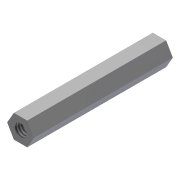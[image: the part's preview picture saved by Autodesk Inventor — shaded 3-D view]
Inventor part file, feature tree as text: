
AUTODESK INVENTOR PART (.ipt)
format: ipt  version: 2013 (Build 170138000, 138)  size: 79,872 bytes
history: native  units: in
note: dims shown in document units (in); Inventor stores cm internally (conversion verified against a paired STEP export)
features: sketch x2, extrude x1, hole x1, mirror x1
ambient origin geometry x8: Origin, YZ Plane, XZ Plane, XY Plane, X Axis, Y Axis, Z Axis, Center Point
bodies: Solid1 (feature_tree)
feature tree (5):
  extrude  "Extrusion1"  Depth=1.5in TaperAngle=0.0deg
  hole  "Hole1"  [1 undecoded]
  mirror  "Mirror1"
  sketch  "Sketch1"  dims[d0=0.25in d1=1.5in d2=0.0in]
  sketch  "Sketch2"  dims[d3=0.13in d4=0.375in d5=0.375in d6=0.25in d7=0.5635in d8=0.375in d9=0.0in]
note: 1 required parameter value undecoded (feature->parameter linkage not recoverable at this tier; creation-order binding heuristic only, values carry confidence <= 0.55)
